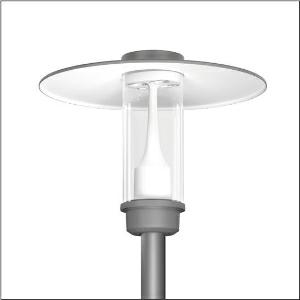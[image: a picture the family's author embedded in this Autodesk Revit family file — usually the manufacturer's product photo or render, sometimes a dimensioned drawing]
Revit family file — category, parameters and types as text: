
# Revit family: litepole_2_iq___p1_0a_5xa5425bf14h_a5ac
name_source: partatom
category: Lighting Fixtures
units: mm (PartAtom-declared; Revit-internal decimal feet)

## family parameters
Cut with Voids When Loaded = No
Host = Face
Light Source = No
Part Type = Normal
Room Calculation Point = No
Round Connector Dimension = Use Diameter
Shared = No

## types (1)
- --- (1 x LED, 1520 lm, 12.9 W, 2200K)
    Apparent Load = 13 VA
    CIE Flux Codes = 33 62 89 96 100
    Color Rendering = 70
    Color Temperature = 2200K
    Default Elevation = 1800 mm
    Description = Litepole 2 iQ, mast luminaire, Module 540 iQ-SR, primary light control with 3 zone facetted reflector, of plastic, silver coated, highly specular, structured, primary optical cover: cover, of PMMA, transparent, light distribution: P1.0a, light emission: direct distribution, primary light characteristic: strongly asymmetric, installation type: post-top, LED, High Power LED, rated luminous flux: 1.520lm, luminous efficacy: 118lm/W, light colour: 722, colour temperature: 2200K, control gear: ECG iQ, control: pre-setting: logarithmic dimming characteristic, Street-Remote, Auto-Match, Temp-Guard, Lumen-Switch, Night-Set, Smart-Wire, Light-Fading, Desk-Remote (wireless, voltage-free reading and setting of iQ features in the workshop via application-optimized NFC function/RFID function), optimised constant luminous flux control (CLO 2.0), with terminal, 6-pole, max. 2.5mm², mains connection: 230..240V, AC, 50/60Hz, start of lifetime: 13W, end of service life: 13W, reduction: 6W, luminaire housing, upper part, of aluminium, coated, Siteco® metallic grey (DB 702S), diameter: 750mm, height: 590mm, spigot size: d x l = 76 x 70mm (post-top) | with reducer (optional accessory) 60 x 70mm, post-top mast mounting element, of diecast aluminium, coated, Siteco® metallic grey (DB 702S), Module 540 iQ-SR, traffic white (RAL 9016), equipment: standard, protection rating (complete): IP65, insulation class (complete): insulation class II (safety insulation), certification: CE, ENEC, VDE, packaging unit: 1 piece

Light Distribution: P1.0a
    Height = 590 mm
    Lamp = 1 x LED
    Lamp Light Flux = 1520 lm
    Lamp Power = 12.9 W
    Lamp count = 1
    Length = 750 mm
    Luminous efficacy = 118 lm/W
    Manufacturer = Siteco
    ModVariant = No
    Model = 5XA5425BF14H
    Number of Poles = 1
    OnlyDefault = Yes
    Power Factor = 1
    Product Name = Litepole 2 iQ | P1.0a
    Product group = mast luminaire | pylon top
    ProductGroupID = 6100
    Protection Class = Protection class II
    Protection Degree = IP 65
    RLX_Detail_Level = 1
    RLX_Emergency_Light_Flux = 0 lm
    RLX_Emergency_Type = 0
    RLX_Emergency_Type_DB = No
    RlxData = <blob elided: 140045 chars, md5=8495e411>
    Socket = socket
    Standby Power = 0 W
    System Light Flux = 1520 lm
    System Power = 13 W
    Type Comments = factory setting: luminous flux: 100 % | dim-lin: 254 | 516 mA
    Type Image = l_1006518.jpg
    URL = http://relux.com
    VarID = @adj_165229
    Voltage = 0 V
    Weight = 0.00 kg
    Width = 0 mm  [stored 0 ft]

note: [stored X ft] marks values corroborated as IEEE doubles in the binary element streams (Revit-internal decimal feet)

## geometry (parser evidence)
native form markers: Blend x4, Sweep x11
no freeform markers — native parametric forms only
